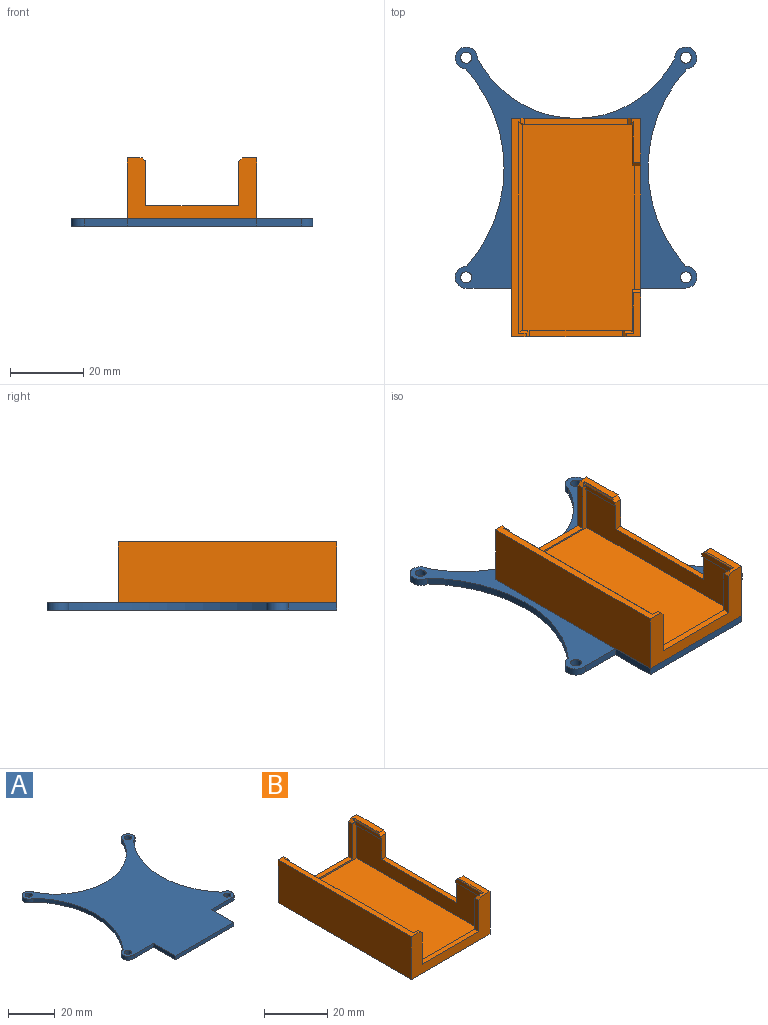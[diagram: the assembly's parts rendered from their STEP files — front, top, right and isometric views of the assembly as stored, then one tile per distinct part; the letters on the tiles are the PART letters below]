
ASSEMBLY  parts=2 mates=1
PART A: 18 faces, bbox 66x79.2x2 mm
  f0: cylinder r=3mm len=5.99mm, axis (0,0,-1), area 27.7mm2, adj f1,f14,f16,f17
  f1: cylinder r=40mm len=53.93mm, axis (0,0,-1), area 118.4mm2, adj f0,f2,f16,f17
  f2: cylinder r=3mm len=6mm, axis (0,0,-1), area 20.4mm2, adj f1,f3,f16,f17
  f3: plane 11.6x2mm, normal (0,-1,0), area 23.2mm2, adj f2,f4,f16,f17
  f4: plane 13.37x2mm, normal (-1,0,0), area 26.7mm2, adj f3,f5,f16,f17
  f5: plane 35.3x2mm, normal (0,-1,0), area 70.6mm2, adj f4,f6,f16,f17
  f6: plane 13.37x2mm, normal (1,0,0), area 26.7mm2, adj f5,f7,f16,f17
  f7: plane 12.31x2mm, normal (0,-1,0), area 24.6mm2, adj f6,f8,f16,f17
  f8: cylinder r=3mm len=5.99mm, axis (0,0,-1), area 18.9mm2, adj f7,f9,f16,f17
  f9: cylinder r=40mm len=53.84mm, axis (0,0,-1), area 118.1mm2, adj f8,f10,f16,f17
  f10: cylinder r=3mm len=5.99mm, axis (0,0,-1), area 27.7mm2, adj f9,f14,f16,f17
  f11: cylinder r=1.5mm len=3mm, axis (0,0,-1), area 18.8mm2, adj f16,f17
  f12: cylinder r=1.5mm len=3mm, axis (0,0,-1), area 18.8mm2, adj f16,f17
  f13: cylinder r=1.5mm len=3mm, axis (0,0,-1), area 18.8mm2, adj f16,f17
  f14: cylinder r=30.3mm len=53.94mm, axis (0,0,-1), area 133mm2, adj f0,f10,f16,f17
  f15: cylinder r=1.5mm len=3mm, axis (0,0,-1), area 18.8mm2, adj f16,f17
  f16: plane 79.18x65.96mm, normal (0,0,1), area 2886.9mm2, adj f0,f1,f2,f3,f4,f5,f6,f7
  f17: plane 79.18x65.96mm, normal (0,0,-1), area 2886.9mm2, adj f0,f1,f2,f3,f4,f5,f6,f7
PART B: 43 faces, bbox 35.3x59.7x16.6 mm
  f0: plane 12x2.5mm, normal (0,0,1), area 24.5mm2, adj f2,f7,f37,f38,f39,f40
  f1: plane 56.1x13.1mm, normal (-1,0,0), area 465.3mm2, adj f5,f10,f12,f19,f20,f21,f25,f26
  f2: plane 59.7x16.6mm, normal (1,0,0), area 653mm2, adj f0,f3,f4,f7,f11,f19,f20,f21
  f3: plane 12x4mm, normal (0,0,1), area 26mm2, adj f2,f4,f33,f34,f35,f36
  f4: plane 35.3x16.6mm, normal (0,-1,0), area 253.5mm2, adj f2,f3,f6,f8,f11,f16,f17,f18
  f5: plane 31.7x14.8mm, normal (0,1,0), area 140mm2, adj f1,f9,f12,f16,f17,f18,f22,f23
  f6: plane 59.7x4mm, normal (0,0,1), area 121.9mm2, adj f4,f7,f8,f28,f29,f30,f31,f32
  f7: plane 35.3x16.6mm, normal (0,1,0), area 171.8mm2, adj f0,f2,f6,f8,f11,f13,f14,f15
  f8: plane 59.7x16.6mm, normal (-1,0,0), area 991mm2, adj f4,f6,f7,f11
  f9: plane 56.1x12.73mm, normal (1,0,0), area 714.2mm2, adj f5,f10,f12,f23
  f10: plane 31.7x15.01mm, normal (0,-1,0), area 60.7mm2, adj f1,f9,f12,f13,f14,f15,f22,f23
  f11: plane 59.7x35.3mm, normal (0,0,-1), area 2107.4mm2, adj f2,f4,f7,f8
  f12: plane 56.1x31.7mm, normal (0,0,1), area 1778.4mm2, adj f1,f5,f9,f10
  f13: plane 28.3x1.8mm, normal (0,0,1), area 50.9mm2, adj f7,f10,f14,f15
  f14: plane 13.6x1.8mm, normal (1,0,0), area 24.5mm2, adj f7,f10,f13,f32
  f15: plane 13.6x1.8mm, normal (-1,0,0), area 24.5mm2, adj f7,f10,f13,f37
  f16: plane 12.1x1.8mm, normal (1,0,0), area 21.8mm2, adj f4,f5,f17,f28
  f17: plane 25.3x1.8mm, normal (0,0,1), area 45.5mm2, adj f4,f5,f16,f18
  f18: plane 12.1x1.8mm, normal (-1,0,0), area 21.8mm2, adj f4,f5,f17,f36
  f19: plane 9x2.3mm, normal (0,1,0), area 16.7mm2, adj f1,f2,f20,f26,f27,f33
  f20: plane 33.7x1.8mm, normal (0,0,1), area 60.7mm2, adj f1,f2,f19,f21
  f21: plane 9x2.3mm, normal (0,-1,0), area 16.7mm2, adj f1,f2,f20,f24,f25,f40
  f22: plane 56.1x0.67mm, normal (1,0,0), area 37.6mm2, adj f5,f10,f30,f42
  f23: plane 56.1x0.5mm, normal (0,0,-1), area 28mm2, adj f5,f9,f10,f42
  f24: plane 11.2x1.4mm, normal (-1,0,0), area 15.6mm2, adj f10,f21,f25,f40,f41
  f25: plane 11.2x0.5mm, normal (0,0,-1), area 5.6mm2, adj f1,f10,f21,f24
  f26: plane 11.2x0.5mm, normal (0,0,-1), area 5.6mm2, adj f1,f5,f19,f27
  f27: plane 11.2x1.7mm, normal (-1,0,0), area 18.8mm2, adj f5,f19,f26,f33,f34
  f28: plane 1.8x1mm, normal (0.71,0,0.71), area 2.1mm2, adj f4,f5,f6,f16,f29
  f29: plane 2.8x0.8mm, normal (0,0.71,0.71), area 2.3mm2, adj f5,f6,f28,f30
  f30: plane 57.7x1mm, normal (0.71,0,0.71), area 80.2mm2, adj f5,f6,f10,f22,f29,f31
  f31: plane 1.3x0.8mm, normal (0,-0.71,0.71), area 0.6mm2, adj f6,f10,f30,f32
  f32: plane 1.8x1mm, normal (0.71,0,0.71), area 2.1mm2, adj f6,f7,f10,f14,f31
  f33: plane 2.3x1mm, normal (0,0.71,0.71), area 3.2mm2, adj f2,f3,f19,f27,f34
  f34: plane 11.3x0.8mm, normal (-0.71,0,0.71), area 4.8mm2, adj f3,f5,f27,f33,f35
  f35: plane 2.8x0.8mm, normal (0,0.71,0.71), area 2.3mm2, adj f3,f5,f34,f36
  f36: plane 1.8x1mm, normal (-0.71,0,0.71), area 2.1mm2, adj f3,f4,f5,f18,f35
  f37: plane 1.8x1mm, normal (-0.71,0,0.71), area 2.1mm2, adj f0,f7,f10,f15,f38
  f38: plane 1.3x0.8mm, normal (0,-0.71,0.71), area 0.6mm2, adj f0,f10,f37,f39
  f39: plane 11.09x0.8mm, normal (-0.71,0,0.71), area 1.7mm2, adj f0,f10,f38,f40,f41
  f40: plane 2.3x1mm, normal (0,-0.71,0.71), area 3.1mm2, adj f0,f2,f21,f24,f39,f41
  f41: plane 10.8x0.51mm, normal (-0.92,0,0.38), area 5.8mm2, adj f10,f24,f39,f40
  f42: plane 56.1x0.7mm, normal (0.71,0,-0.71), area 55.5mm2, adj f5,f10,f22,f23
PLACE A t=(44.93,53.22,-2.24)mm fixed
PLACE B t=(-17.77,-37.92,-0.24)mm
MATE fastened B.f11 <-> A.f16  axis (0,0,-1) through (-0.12,-37.92,-0.24)mm
